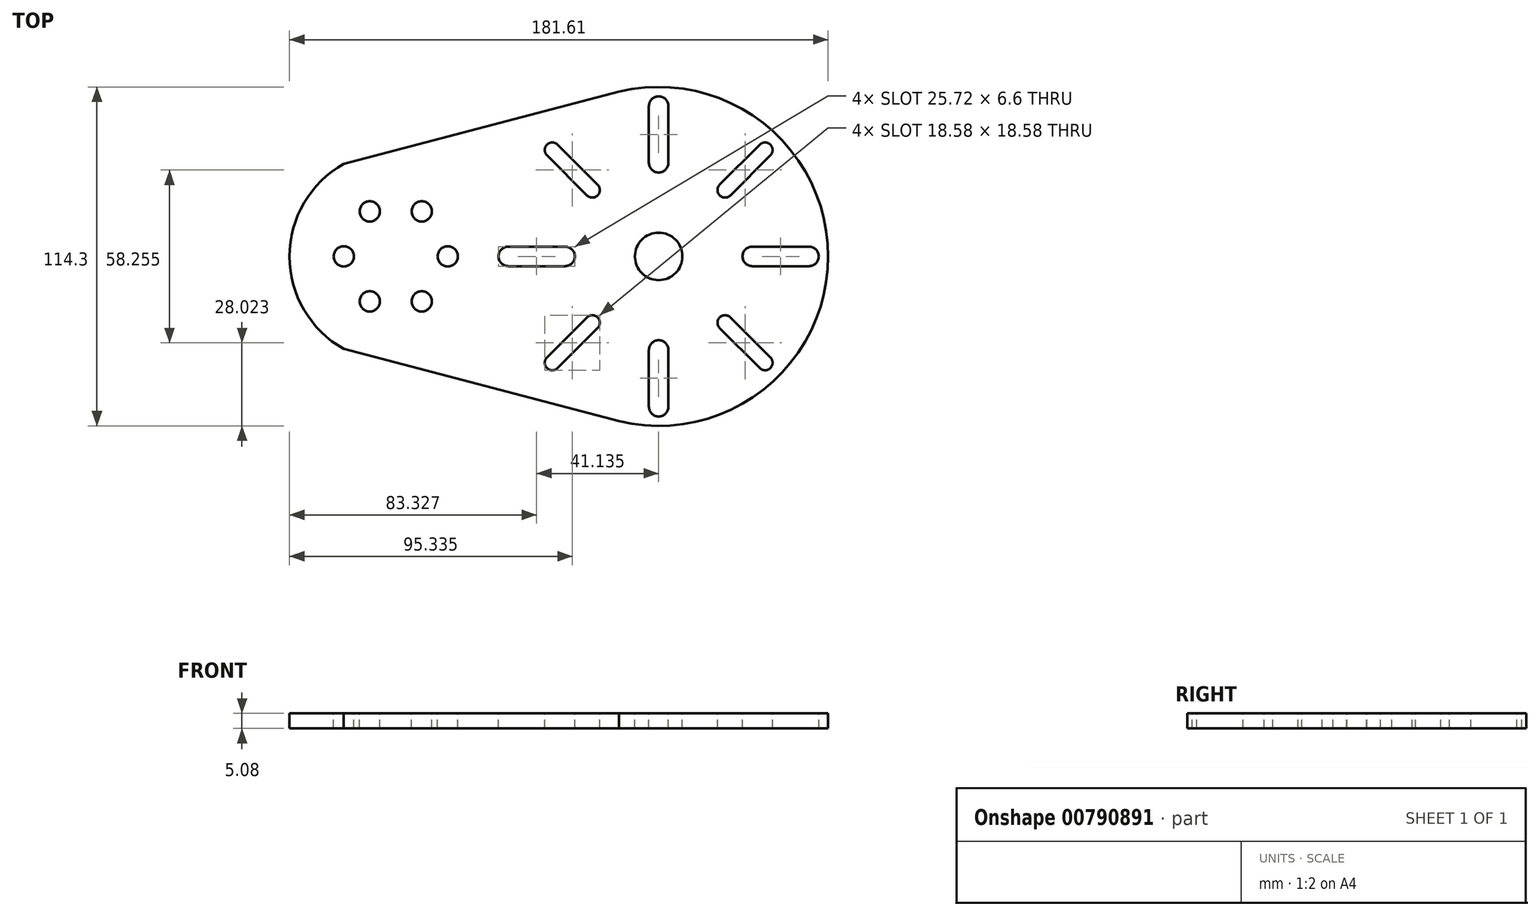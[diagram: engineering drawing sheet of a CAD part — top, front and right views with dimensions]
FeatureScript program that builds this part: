
annotation { "Feature Type Name" : "Feature", "Feature Type Description" : "" }
export const myFeature = defineFeature(function(context is Context, id is Id, definition is map)
    precondition{}
    {
        {
            var Q0;
            Q0=qCreatedBy(makeId("Top.planeOp"),FACE);
            var sketch = newSketch(context, id + "F0", { "sketchPlane" : qUnion([Q0])});
            skLineSegment(sketch, "E0", {"start": v(0, 0) * mm, "end": v(-58.93, 0) * mm, "construction": true});
            skPoint(sketch, "E1", {"position": v(-29.46, 0) * mm});
            skCircle(sketch, "E2", {"center": v(-29.46, 0) * mm, "radius": 29.46 * mm, "construction": true});
            skCircle(sketch, "E3", {"center": v(-29.46, 0) * mm, "radius": 17.53 * mm, "construction": true});
            skPoint(sketch, "E4", {"position": v(59.18, 0) * mm});
            skPoint(sketch, "E5", {"position": v(-11.94, 0) * mm});
            skCircle(sketch, "E6", {"center": v(59.18, 0) * mm, "radius": 19.05 * mm, "construction": true});
            skCircle(sketch, "E7", {"center": v(59.18, 0) * mm, "radius": 31.75 * mm, "construction": true});
            skCircle(sketch, "E8", {"center": v(-11.94, 0) * mm, "radius": 3.43 * mm});
            skCircle(sketch, "E9.1.0", {"center": v(-20.7, 15.18) * mm, "radius": 3.43 * mm});
            skCircle(sketch, "E9.2.0", {"center": v(-38.23, 15.18) * mm, "radius": 3.43 * mm});
            skCircle(sketch, "E9.3.0", {"center": v(-46.99, 0) * mm, "radius": 3.43 * mm});
            skCircle(sketch, "E9.4.0", {"center": v(-38.23, -15.18) * mm, "radius": 3.43 * mm});
            skCircle(sketch, "E9.5.0", {"center": v(-20.7, -15.18) * mm, "radius": 3.43 * mm});
            skCircle(sketch, "E10", {"center": v(-29.46, 0) * mm, "radius": 10.16 * mm, "construction": true});
            skCircle(sketch, "E11", {"center": v(-29.46, 0) * mm, "radius": 35.81 * mm, "construction": true});
            skArc(sketch, "E12", {"start": v(92.4, -46.5) * mm, "mid": v(116.33, 0) * mm, "end": v(92.4, 46.5) * mm, "construction": true});
            skPoint(sketch, "E13", {"position": v(-29.46, 35.81) * mm});
            skPoint(sketch, "E14", {"position": v(-29.46, -35.81) * mm});
            skPoint(sketch, "E15", {"position": v(59.18, 57.15) * mm});
            skPoint(sketch, "E16", {"position": v(59.18, -57.15) * mm});
            skPoint(sketch, "E17", {"position": v(-65.28, 0) * mm});
            skCircle(sketch, "E18", {"center": v(59.18, 0) * mm, "radius": 47 * mm, "construction": true});
            skLineSegment(sketch, "E19", {"start": v(59.18, 0) * mm, "end": v(116.33, 0) * mm, "construction": true});
            skLineSegment(sketch, "E20", {"start": v(59.18, 0) * mm, "end": v(99.6, 40.41) * mm, "construction": true});
            skCircle(sketch, "E21", {"center": v(59.18, 0) * mm, "radius": 8 * mm});
            skArc(sketch, "E22.converted", {"start": v(92.4, 46.5) * mm, "mid": v(2.03, 0) * mm, "end": v(92.4, -46.5) * mm, "construction": true});
            skCircle(sketch, "E23", {"center": v(59.18, 0) * mm, "radius": 50.8 * mm, "construction": true});
            skLineSegment(sketch, "E24", {"start": v(83.36, 20.58) * mm, "end": v(96.85, 34.08) * mm});
            skLineSegment(sketch, "E25", {"start": v(79.76, 24.17) * mm, "end": v(93.26, 37.67) * mm});
            skPoint(sketch, "E26.orphan", {"position": v(90.93, 0) * mm});
            skLineSegment(sketch, "E27", {"start": v(90.76, 3.3) * mm, "end": v(109.87, 3.3) * mm});
            skLineSegment(sketch, "E28", {"start": v(90.76, -3.3) * mm, "end": v(109.87, -3.3) * mm});
            skArc(sketch, "E29", {"start": v(109.87, 3.3) * mm, "mid": v(113.18, 0) * mm, "end": v(109.87, -3.3) * mm});
            skArc(sketch, "E30", {"start": v(90.76, 3.3) * mm, "mid": v(87.46, 0) * mm, "end": v(90.76, -3.3) * mm});
            skArc(sketch, "E31", {"start": v(79.76, 24.17) * mm, "mid": v(79.76, 20.58) * mm, "end": v(83.36, 20.58) * mm});
            skArc(sketch, "E32", {"start": v(93.26, 37.67) * mm, "mid": v(96.85, 37.67) * mm, "end": v(96.85, 34.08) * mm});
            skLineSegment(sketch, "E33.1.0", {"start": v(62.48, -31.58) * mm, "end": v(62.48, -50.7) * mm});
            skArc(sketch, "E33.1.1", {"start": v(62.48, -31.58) * mm, "mid": v(59.18, -28.28) * mm, "end": v(55.88, -31.58) * mm});
            skLineSegment(sketch, "E33.1.2", {"start": v(55.88, -31.58) * mm, "end": v(55.88, -50.7) * mm});
            skArc(sketch, "E33.1.3", {"start": v(62.48, -50.7) * mm, "mid": v(59.18, -54) * mm, "end": v(55.88, -50.7) * mm});
            skArc(sketch, "E33.1.4", {"start": v(83.36, -20.58) * mm, "mid": v(79.76, -20.58) * mm, "end": v(79.76, -24.17) * mm});
            skLineSegment(sketch, "E33.1.5", {"start": v(79.76, -24.17) * mm, "end": v(93.26, -37.67) * mm});
            skArc(sketch, "E33.1.6", {"start": v(96.85, -34.08) * mm, "mid": v(96.85, -37.67) * mm, "end": v(93.26, -37.67) * mm});
            skLineSegment(sketch, "E33.1.7", {"start": v(83.36, -20.58) * mm, "end": v(96.85, -34.08) * mm});
            skLineSegment(sketch, "E33.2.0", {"start": v(27.6, -3.3) * mm, "end": v(8.49, -3.3) * mm});
            skArc(sketch, "E33.2.1", {"start": v(27.6, -3.3) * mm, "mid": v(30.9, 0) * mm, "end": v(27.6, 3.3) * mm});
            skLineSegment(sketch, "E33.2.2", {"start": v(27.6, 3.3) * mm, "end": v(8.49, 3.3) * mm});
            skArc(sketch, "E33.2.3", {"start": v(8.49, -3.3) * mm, "mid": v(5.19, 0) * mm, "end": v(8.49, 3.3) * mm});
            skArc(sketch, "E33.2.4", {"start": v(38.6, -24.17) * mm, "mid": v(38.6, -20.58) * mm, "end": v(35, -20.58) * mm});
            skLineSegment(sketch, "E33.2.5", {"start": v(35, -20.58) * mm, "end": v(21.5, -34.08) * mm});
            skArc(sketch, "E33.2.6", {"start": v(25.1, -37.67) * mm, "mid": v(21.5, -37.67) * mm, "end": v(21.5, -34.08) * mm});
            skLineSegment(sketch, "E33.2.7", {"start": v(38.6, -24.17) * mm, "end": v(25.1, -37.67) * mm});
            skLineSegment(sketch, "E33.3.0", {"start": v(55.88, 31.58) * mm, "end": v(55.88, 50.7) * mm});
            skArc(sketch, "E33.3.1", {"start": v(55.88, 31.58) * mm, "mid": v(59.18, 28.28) * mm, "end": v(62.48, 31.58) * mm});
            skLineSegment(sketch, "E33.3.2", {"start": v(62.48, 31.58) * mm, "end": v(62.48, 50.7) * mm});
            skArc(sketch, "E33.3.3", {"start": v(55.88, 50.7) * mm, "mid": v(59.18, 54) * mm, "end": v(62.48, 50.7) * mm});
            skArc(sketch, "E33.3.4", {"start": v(35, 20.58) * mm, "mid": v(38.6, 20.58) * mm, "end": v(38.6, 24.17) * mm});
            skLineSegment(sketch, "E33.3.5", {"start": v(38.6, 24.17) * mm, "end": v(25.1, 37.67) * mm});
            skArc(sketch, "E33.3.6", {"start": v(21.5, 34.08) * mm, "mid": v(21.5, 37.67) * mm, "end": v(25.1, 37.67) * mm});
            skLineSegment(sketch, "E33.3.7", {"start": v(35, 20.58) * mm, "end": v(21.5, 34.08) * mm});
            skLineSegment(sketch, "E33.anchor1", {"start": v(59.18, 0) * mm, "end": v(109.87, 0) * mm, "construction": true});
            skLineSegment(sketch, "E33.anchor2", {"start": v(59.18, 0) * mm, "end": v(59.18, 50.7) * mm, "construction": true});
            skPoint(sketch, "E34", {"position": v(45.8, -55.56) * mm});
            skPoint(sketch, "E35", {"position": v(45.8, 55.56) * mm});
            skLineSegment(sketch, "E36", {"start": v(-47.05, -31.2) * mm, "end": v(45.8, -55.56) * mm});
            skLineSegment(sketch, "E37", {"start": v(45.8, 55.56) * mm, "end": v(-47.05, 31.2) * mm});
            skArc(sketch, "E38", {"start": v(-47.05, 31.2) * mm, "mid": v(-65.28, 0) * mm, "end": v(-47.05, -31.2) * mm});
            skArc(sketch, "E39", {"start": v(45.8, -55.56) * mm, "mid": v(116.33, 0) * mm, "end": v(45.8, 55.56) * mm});
            skSolve(sketch);
        }
        {
            var Q0;
            Q0=makeQuery(id+"F0.imprint","IMPRINT",FACE,{"disambiguationData":[TD([[makeQuery(id+"F0.imprint","IMPRINT",EDGE,{"derivedFrom":sQuery(id+"F0.wireOp",EDGE,"E8")}),-1.0]])]});
            extrude(context, id + "F1", {"entities" : qUnion([Q0]), "oppositeDirection" : true, "depth" : 5.08 * mm, "offsetDistance" : 25.4 * mm});
        }
    });
